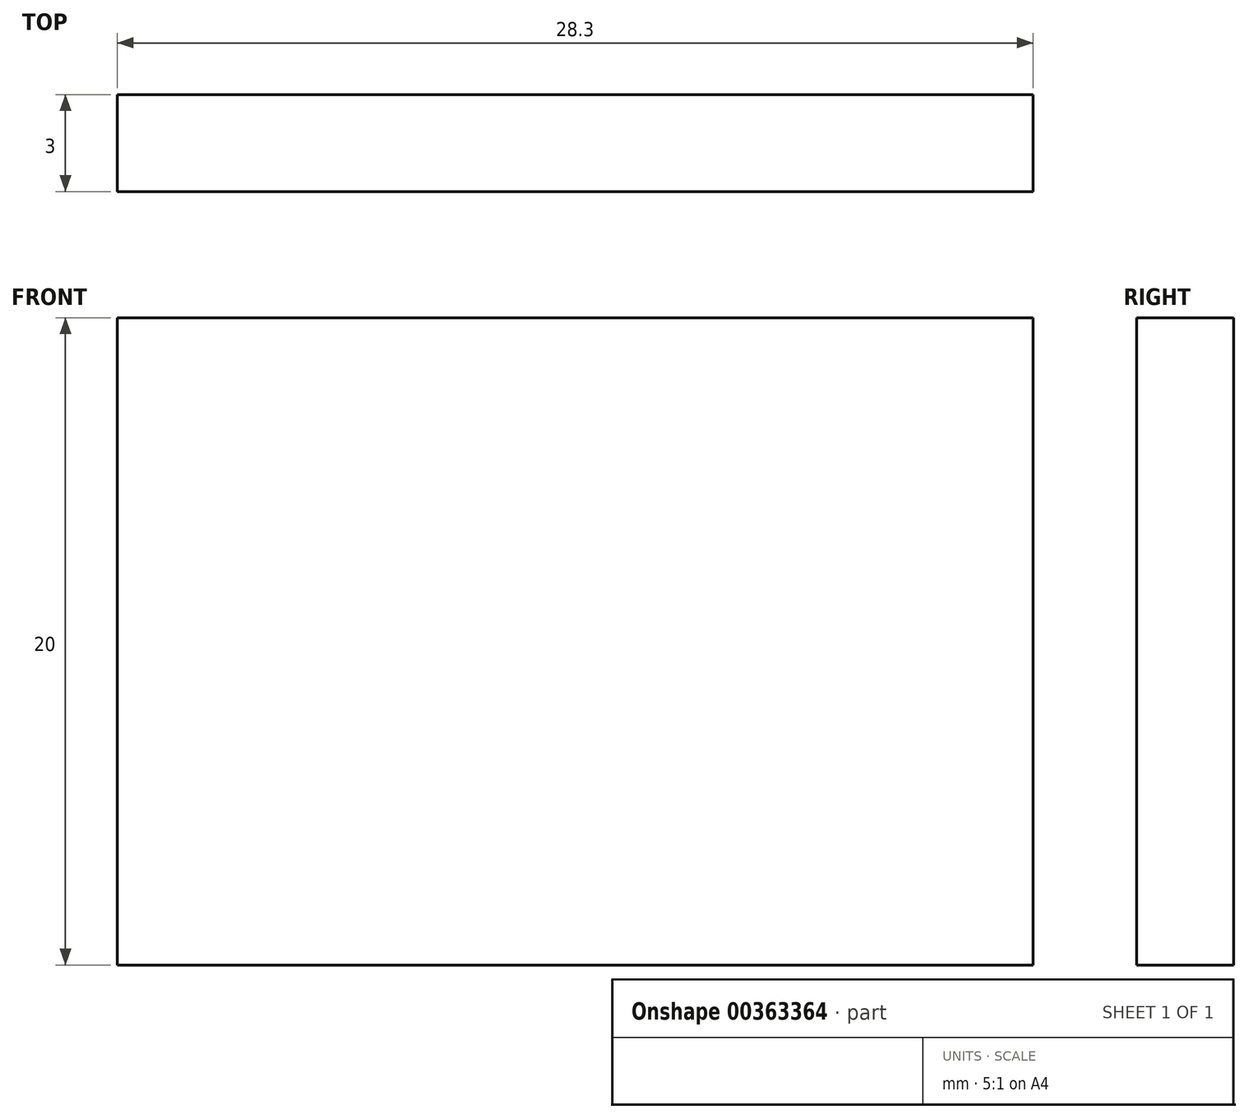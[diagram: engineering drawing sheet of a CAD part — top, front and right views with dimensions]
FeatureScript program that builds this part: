
annotation { "Feature Type Name" : "Feature", "Feature Type Description" : "" }
export const myFeature = defineFeature(function(context is Context, id is Id, definition is map)
    precondition{}
    {
        {
            var Q0;
            Q0=qCreatedBy(makeId("Front.planeOp"),FACE);
            var sketch = newSketch(context, id + "F0", { "sketchPlane" : qUnion([Q0])});
            skLineSegment(sketch, "E0.bottom", {"start": v(0, 0) * mm, "end": v(28.3, 0) * mm});
            skLineSegment(sketch, "E0.top", {"start": v(0, 20) * mm, "end": v(28.3, 20) * mm});
            skLineSegment(sketch, "E0.left", {"start": v(0, 0) * mm, "end": v(0, 20) * mm});
            skLineSegment(sketch, "E0.right", {"start": v(28.3, 0) * mm, "end": v(28.3, 20) * mm});
            skSolve(sketch);
        }
        {
            var Q0;
            Q0=makeQuery(id+"F0.imprint","IMPRINT",FACE,{"disambiguationData":[TD([[makeQuery(id+"F0.imprint","IMPRINT",EDGE,{"derivedFrom":sQuery(id+"F0.wireOp",EDGE,"E0.bottom")}),1.0]])]});
            extrude(context, id + "F1", {"entities" : qUnion([Q0]), "depth" : 3 * mm});
        }
    });
